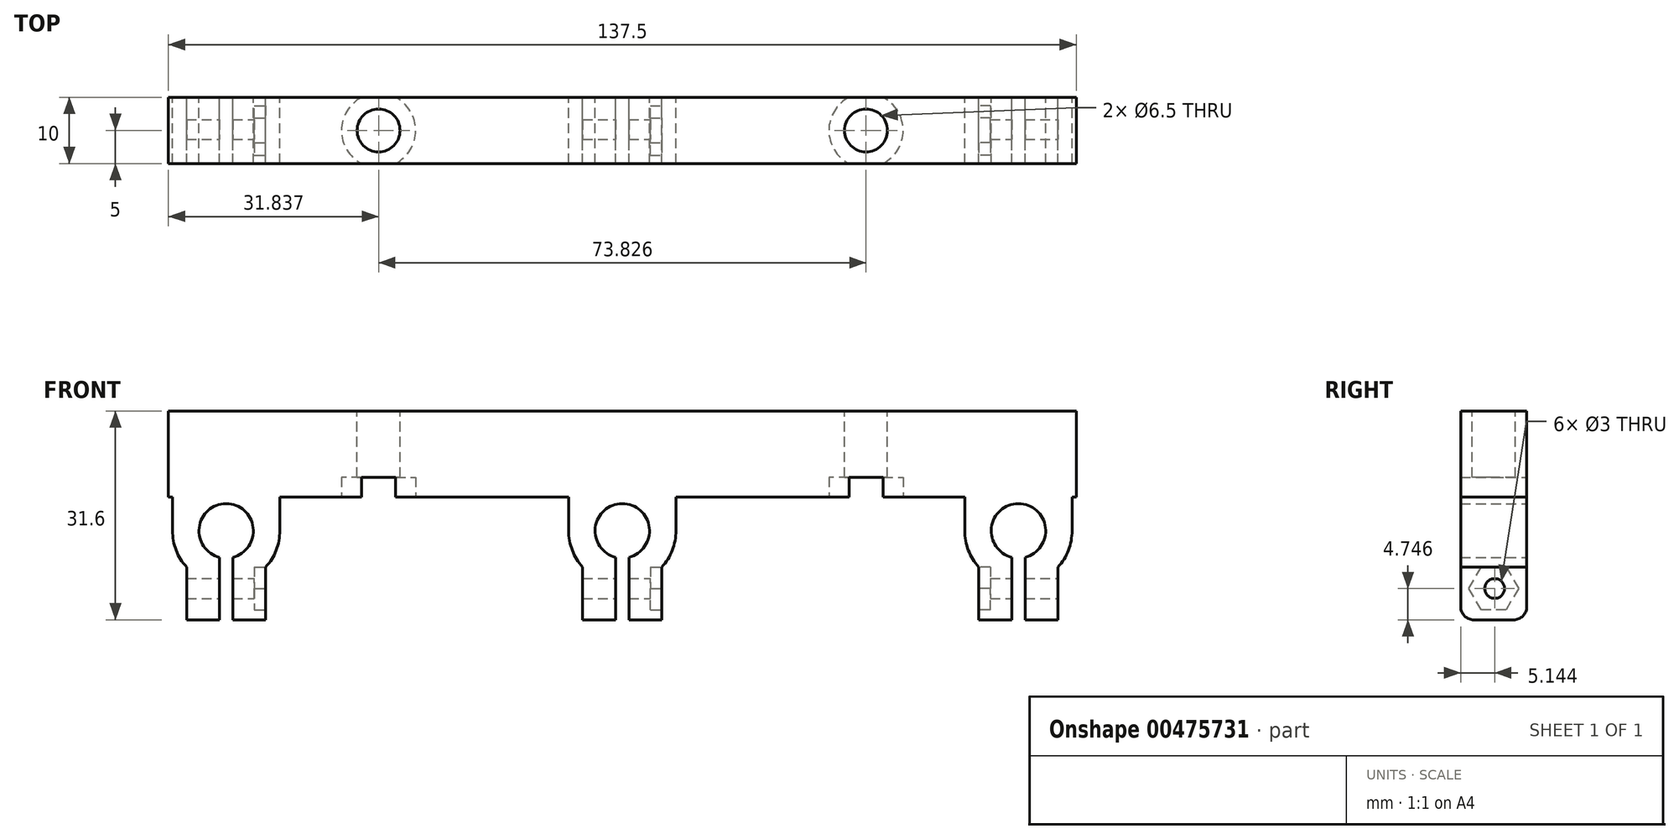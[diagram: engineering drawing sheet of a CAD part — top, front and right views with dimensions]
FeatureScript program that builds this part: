
annotation { "Feature Type Name" : "Feature", "Feature Type Description" : "" }
export const myFeature = defineFeature(function(context is Context, id is Id, definition is map)
    precondition{}
    {
        {
            var Q0;
            Q0=qCreatedBy(makeId("Top.planeOp"),FACE);
            var sketch = newSketch(context, id + "F0", { "sketchPlane" : qUnion([Q0])});
            skLineSegment(sketch, "E0.bottom", {"start": v(68.75, -5) * mm, "end": v(-68.75, -5) * mm});
            skLineSegment(sketch, "E0.top", {"start": v(68.75, 5) * mm, "end": v(-68.75, 5) * mm});
            skLineSegment(sketch, "E0.left", {"start": v(68.75, -5) * mm, "end": v(68.75, 5) * mm});
            skLineSegment(sketch, "E0.right", {"start": v(-68.75, -5) * mm, "end": v(-68.75, 5) * mm});
            skPoint(sketch, "E0.middle", {"position": v(0, 0) * mm});
            skSolve(sketch);
        }
        {
            var Q0;
            Q0=qSketchRegion(id+"F0",true);
            extrude(context, id + "F1", {"entities" : qUnion([Q0]), "depth" : 9 * mm});
        }
        {
            var Q0;
            Q0=makeQuery(id+"F1.opExtrude","SWEPT_FACE",FACE,{"disambiguationData":[OSD([sQuery(id+"F0.wireOp",EDGE,"E0.top")])]});
            var sketch = newSketch(context, id + "F2", { "sketchPlane" : qUnion([Q0])});
            skCircle(sketch, "E1", {"center": v(0, -9.13) * mm, "radius": 4.12 * mm});
            skPoint(sketch, "E1.centerSnap0", {"position": v(0, 0) * mm});
            skCircle(sketch, "E2", {"center": v(-60, -9.12) * mm, "radius": 4.12 * mm});
            skCircle(sketch, "E3", {"center": v(60, -9.13) * mm, "radius": 4.12 * mm});
            skLineSegment(sketch, "E4", {"start": v(60, -9.13) * mm, "end": v(0, -9.13) * mm, "construction": true});
            skLineSegment(sketch, "E5", {"start": v(-60, -9.12) * mm, "end": v(0, -9.13) * mm, "construction": true});
            skArc(sketch, "E6", {"start": v(-68.12, -9.12) * mm, "mid": v(-60, -17.25) * mm, "end": v(-51.88, -9.12) * mm});
            skLineSegment(sketch, "E7", {"start": v(-68.12, -9.12) * mm, "end": v(-51.88, -9.12) * mm, "construction": true});
            skArc(sketch, "E8", {"start": v(-8.12, -9.13) * mm, "mid": v(0, -17.25) * mm, "end": v(8.12, -9.13) * mm});
            skLineSegment(sketch, "E9", {"start": v(-8.12, -9.12) * mm, "end": v(8.12, -9.13) * mm, "construction": true});
            skArc(sketch, "E10", {"start": v(51.88, -9.13) * mm, "mid": v(60, -17.25) * mm, "end": v(68.12, -9.13) * mm});
            skLineSegment(sketch, "E11", {"start": v(51.88, -9.13) * mm, "end": v(68.12, -9.13) * mm, "construction": true});
            skLineSegment(sketch, "E12", {"start": v(-68.12, -9.12) * mm, "end": v(-68.12, -4) * mm});
            skLineSegment(sketch, "E13", {"start": v(-51.88, -9.12) * mm, "end": v(-51.88, -4) * mm});
            skLineSegment(sketch, "E14", {"start": v(-8.12, -9.13) * mm, "end": v(-8.12, -4) * mm});
            skLineSegment(sketch, "E15", {"start": v(8.12, -9.13) * mm, "end": v(8.12, -4) * mm});
            skLineSegment(sketch, "E16", {"start": v(51.88, -9.13) * mm, "end": v(51.88, -4) * mm});
            skLineSegment(sketch, "E17", {"start": v(68.12, -9.13) * mm, "end": v(68.12, -4) * mm});
            skLineSegment(sketch, "E18", {"start": v(68.12, -4) * mm, "end": v(68.75, -4) * mm});
            skLineSegment(sketch, "E19", {"start": v(68.75, -4) * mm, "end": v(68.75, 0) * mm});
            skLineSegment(sketch, "E20", {"start": v(51.88, -4) * mm, "end": v(8.12, -4) * mm});
            skLineSegment(sketch, "E21", {"start": v(-8.12, -4) * mm, "end": v(-51.88, -4) * mm});
            skLineSegment(sketch, "E22", {"start": v(-68.12, -4) * mm, "end": v(-68.75, -4) * mm});
            skLineSegment(sketch, "E23", {"start": v(-68.75, -4) * mm, "end": v(-68.75, 0) * mm});
            skLineSegment(sketch, "E24.bottom", {"start": v(66, -14.6) * mm, "end": v(54, -14.6) * mm, "construction": true});
            skLineSegment(sketch, "E24.top", {"start": v(66, -22.6) * mm, "end": v(54, -22.6) * mm});
            skLineSegment(sketch, "E24.left", {"start": v(66, -14.6) * mm, "end": v(66, -22.6) * mm});
            skLineSegment(sketch, "E24.right", {"start": v(54, -14.6) * mm, "end": v(54, -22.6) * mm});
            skLineSegment(sketch, "E25.bottom", {"start": v(6, -14.6) * mm, "end": v(-6, -14.6) * mm, "construction": true});
            skLineSegment(sketch, "E25.top", {"start": v(6, -22.6) * mm, "end": v(-6, -22.6) * mm});
            skLineSegment(sketch, "E25.left", {"start": v(6, -14.6) * mm, "end": v(6, -22.6) * mm});
            skLineSegment(sketch, "E25.right", {"start": v(-6, -14.6) * mm, "end": v(-6, -22.6) * mm});
            skLineSegment(sketch, "E26.bottom", {"start": v(-54, -14.6) * mm, "end": v(-66, -14.6) * mm, "construction": true});
            skLineSegment(sketch, "E26.top", {"start": v(-54, -22.6) * mm, "end": v(-66, -22.6) * mm});
            skLineSegment(sketch, "E26.left", {"start": v(-54, -14.6) * mm, "end": v(-54, -22.6) * mm});
            skLineSegment(sketch, "E26.right", {"start": v(-66, -14.6) * mm, "end": v(-66, -22.6) * mm});
            skLineSegment(sketch, "E27.bottom", {"start": v(61, -13.13) * mm, "end": v(59, -13.13) * mm});
            skLineSegment(sketch, "E27.top", {"start": v(61, -22.6) * mm, "end": v(59, -22.6) * mm});
            skLineSegment(sketch, "E27.left", {"start": v(61, -13.13) * mm, "end": v(61, -22.6) * mm});
            skLineSegment(sketch, "E27.right", {"start": v(59, -13.13) * mm, "end": v(59, -22.6) * mm});
            skLineSegment(sketch, "E28.bottom", {"start": v(1, -13.13) * mm, "end": v(-1, -13.13) * mm});
            skLineSegment(sketch, "E28.top", {"start": v(1, -22.6) * mm, "end": v(-1, -22.6) * mm});
            skLineSegment(sketch, "E28.left", {"start": v(1, -13.13) * mm, "end": v(1, -22.6) * mm});
            skLineSegment(sketch, "E28.right", {"start": v(-1, -13.13) * mm, "end": v(-1, -22.6) * mm});
            skLineSegment(sketch, "E29.bottom", {"start": v(-59, -13.13) * mm, "end": v(-61, -13.13) * mm});
            skLineSegment(sketch, "E29.top", {"start": v(-59, -22.6) * mm, "end": v(-61, -22.6) * mm});
            skLineSegment(sketch, "E29.left", {"start": v(-59, -13.13) * mm, "end": v(-59, -22.6) * mm});
            skLineSegment(sketch, "E29.right", {"start": v(-61, -13.13) * mm, "end": v(-61, -22.6) * mm});
            skSolve(sketch);
        }
        {
            var Q0;
            {var subQ0=sQuery(id+"F2.wireOp",EDGE,"E26.right");Q0=makeQuery(id+"F2.imprint","IMPRINT",FACE,{"disambiguationData":[TD([[makeQuery(id+"F2.imprint","IMPRINT",EDGE,{"derivedFrom":subQ0}),1.0]])]});}
            var Q1;
            {var subQ0=sQuery(id+"F2.wireOp",EDGE,"E26.left");Q1=makeQuery(id+"F2.imprint","IMPRINT",FACE,{"disambiguationData":[TD([[makeQuery(id+"F2.imprint","IMPRINT",EDGE,{"derivedFrom":subQ0}),-1.0]])]});}
            var Q2;
            {var subQ0=sQuery(id+"F2.wireOp",EDGE,"E25.right");Q2=makeQuery(id+"F2.imprint","IMPRINT",FACE,{"disambiguationData":[TD([[makeQuery(id+"F2.imprint","IMPRINT",EDGE,{"derivedFrom":subQ0}),1.0]])]});}
            var Q3;
            {var subQ0=sQuery(id+"F2.wireOp",EDGE,"E25.left");Q3=makeQuery(id+"F2.imprint","IMPRINT",FACE,{"disambiguationData":[TD([[makeQuery(id+"F2.imprint","IMPRINT",EDGE,{"derivedFrom":subQ0}),-1.0]])]});}
            var Q4;
            {var subQ0=sQuery(id+"F2.wireOp",EDGE,"E24.right");Q4=makeQuery(id+"F2.imprint","IMPRINT",FACE,{"disambiguationData":[TD([[makeQuery(id+"F2.imprint","IMPRINT",EDGE,{"derivedFrom":subQ0}),1.0]])]});}
            var Q5;
            {var subQ0=sQuery(id+"F2.wireOp",EDGE,"E24.left");Q5=makeQuery(id+"F2.imprint","IMPRINT",FACE,{"disambiguationData":[TD([[makeQuery(id+"F2.imprint","IMPRINT",EDGE,{"derivedFrom":subQ0}),-1.0]])]});}
            var Q6;
            {var subQ3=sQuery(id+"F2.wireOp",EDGE,"E12");Q6=makeQuery(id+"F2.imprint","IMPRINT",FACE,{"disambiguationData":[TD([[makeQuery(id+"F2.imprint","IMPRINT",EDGE,{"derivedFrom":subQ3}),-1.0]])]});}
            var Q7;
            Q7=makeQuery(id+"F1.opExtrude","SWEPT_FACE",FACE,{"disambiguationData":[OSD([sQuery(id+"F0.wireOp",EDGE,"E0.bottom")])]});
            extrude(context, id + "F3", {"entities" : qUnion([Q0, Q1, Q2, Q3, Q4, Q5, Q6]), "operationType" : NewBodyOperationType.ADD, "endBound" : BoundingType.UP_TO_SURFACE, "oppositeDirection" : true, "endBoundEntityFace" : qUnion([Q7]), "depth" : 10 * mm});
        }
        {
            var Q0;
            Q0=makeQuery(id+"F3.opExtrude","SWEPT_FACE",FACE,{"disambiguationData":[OSD([sQuery(id+"F2.wireOp",EDGE,"E26.left")])]});
            var sketch = newSketch(context, id + "F4", { "sketchPlane" : qUnion([Q0])});
            skCircle(sketch, "E30.cCircle", {"center": v(0, -17.85) * mm, "radius": 3.25 * mm, "construction": true});
            skPoint(sketch, "E30.cCircle.centerSnap1", {"position": v(0, -14.6) * mm});
            skLineSegment(sketch, "E30.0", {"start": v(1.88, -14.6) * mm, "end": v(3.75, -17.85) * mm});
            skLineSegment(sketch, "E30.1", {"start": v(3.75, -17.85) * mm, "end": v(1.88, -21.1) * mm});
            skLineSegment(sketch, "E30.2", {"start": v(1.88, -21.1) * mm, "end": v(-1.88, -21.1) * mm});
            skLineSegment(sketch, "E30.3", {"start": v(-1.88, -21.1) * mm, "end": v(-3.75, -17.85) * mm});
            skLineSegment(sketch, "E30.4", {"start": v(-3.75, -17.85) * mm, "end": v(-1.88, -14.6) * mm});
            skLineSegment(sketch, "E30.5", {"start": v(-1.88, -14.6) * mm, "end": v(1.88, -14.6) * mm});
            skPoint(sketch, "E30.0.midPoint", {"position": v(2.81, -16.23) * mm});
            skLineSegment(sketch, "E31.0", {"start": v(5, -14.6) * mm, "end": v(-5, -14.6) * mm});
            skSolve(sketch);
        }
        {
            var Q0;
            Q0=qSketchRegion(id+"F4",true);
            extrude(context, id + "F5", {"entities" : qUnion([Q0]), "operationType" : NewBodyOperationType.REMOVE, "oppositeDirection" : true, "depth" : 1.75 * mm});
        }
        {
            var Q0;
            Q0=makeQuery(id+"F3.opExtrude","SWEPT_FACE",FACE,{"disambiguationData":[OSD([sQuery(id+"F2.wireOp",EDGE,"E25.right")])]});
            var sketch = newSketch(context, id + "F6", { "sketchPlane" : qUnion([Q0])});
            skLineSegment(sketch, "E32.0.0", {"start": v(1.88, -14.6) * mm, "end": v(3.75, -17.85) * mm});
            skLineSegment(sketch, "E32.0.1", {"start": v(3.75, -17.85) * mm, "end": v(1.88, -21.1) * mm});
            skLineSegment(sketch, "E32.0.2", {"start": v(1.88, -21.1) * mm, "end": v(-1.88, -21.1) * mm});
            skLineSegment(sketch, "E32.0.3", {"start": v(-1.88, -21.1) * mm, "end": v(-3.75, -17.85) * mm});
            skLineSegment(sketch, "E32.0.4", {"start": v(-3.75, -17.85) * mm, "end": v(-1.88, -14.6) * mm});
            skLineSegment(sketch, "E32.0.5", {"start": v(-1.88, -14.6) * mm, "end": v(1.88, -14.6) * mm});
            skSolve(sketch);
        }
        {
            var Q0;
            Q0=qSketchRegion(id+"F6",true);
            extrude(context, id + "F7", {"entities" : qUnion([Q0]), "operationType" : NewBodyOperationType.REMOVE, "oppositeDirection" : true, "depth" : 1.75 * mm});
        }
        {
            var Q0;
            Q0=makeQuery(id+"F3.opExtrude","SWEPT_FACE",FACE,{"disambiguationData":[OSD([sQuery(id+"F2.wireOp",EDGE,"E24.right")])]});
            var sketch = newSketch(context, id + "F8", { "sketchPlane" : qUnion([Q0])});
            skLineSegment(sketch, "E33.0.0", {"start": v(-1.88, -14.6) * mm, "end": v(-3.75, -17.85) * mm});
            skLineSegment(sketch, "E33.0.1", {"start": v(-3.75, -17.85) * mm, "end": v(-1.88, -21.1) * mm});
            skLineSegment(sketch, "E33.0.2", {"start": v(-1.88, -21.1) * mm, "end": v(1.88, -21.1) * mm});
            skLineSegment(sketch, "E33.0.3", {"start": v(1.88, -21.1) * mm, "end": v(3.75, -17.85) * mm});
            skLineSegment(sketch, "E33.0.4", {"start": v(3.75, -17.85) * mm, "end": v(1.88, -14.6) * mm});
            skLineSegment(sketch, "E33.0.5", {"start": v(1.88, -14.6) * mm, "end": v(-1.88, -14.6) * mm});
            skSolve(sketch);
        }
        {
            var Q0;
            Q0=qSketchRegion(id+"F8",true);
            extrude(context, id + "F9", {"entities" : qUnion([Q0]), "operationType" : NewBodyOperationType.REMOVE, "oppositeDirection" : true, "depth" : 1.75 * mm});
        }
        {
            var Q0;
            Q0=makeQuery(id+"F3.opExtrude","SWEPT_FACE",FACE,{"disambiguationData":[OSD([sQuery(id+"F2.wireOp",EDGE,"E26.right")])]});
            var sketch = newSketch(context, id + "F10", { "sketchPlane" : qUnion([Q0])});
            skCircle(sketch, "E34", {"center": v(0.14, -17.85) * mm, "radius": 1.5 * mm});
            skPoint(sketch, "E34.centerSnap0", {"position": v(-3.75, -17.85) * mm});
            skSolve(sketch);
        }
        {
            var Q0;
            Q0=qSketchRegion(id+"F10",true);
            extrude(context, id + "F11", {"entities" : qUnion([Q0]), "operationType" : NewBodyOperationType.REMOVE, "endBound" : BoundingType.THROUGH_ALL, "oppositeDirection" : true, "depth" : 25 * mm});
        }
        {
            var Q0;
            Q0=makeQuery(id+"F1.opExtrude","CAP_FACE",FACE,{"disambiguationData":[OSD([sQuery(id+"F0.wireOp",EDGE,"E0.bottom"),sQuery(id+"F0.wireOp",EDGE,"E0.top"),sQuery(id+"F0.wireOp",EDGE,"E0.left"),sQuery(id+"F0.wireOp",EDGE,"E0.right")])],"isStart":false});
            var sketch = newSketch(context, id + "F12", { "sketchPlane" : qUnion([Q0])});
            skCircle(sketch, "E35", {"center": v(36.91, 0) * mm, "radius": 3.25 * mm});
            skLineSegment(sketch, "E36", {"start": v(0, 0) * mm, "end": v(36.91, 0) * mm, "construction": true});
            skCircle(sketch, "E37", {"center": v(-36.91, 0) * mm, "radius": 3.25 * mm});
            skLineSegment(sketch, "E38", {"start": v(0, 0) * mm, "end": v(-36.91, 0) * mm, "construction": true});
            skSolve(sketch);
        }
        {
            var Q0;
            Q0=qSketchRegion(id+"F12",true);
            extrude(context, id + "F13", {"entities" : qUnion([Q0]), "operationType" : NewBodyOperationType.REMOVE, "endBound" : BoundingType.THROUGH_ALL, "oppositeDirection" : true, "depth" : 25 * mm});
        }
        {
            var Q0;
            Q0=makeQuery(id+"F3.opExtrude","SWEPT_FACE",FACE,{"disambiguationData":[OSD([sQuery(id+"F2.wireOp",EDGE,"E26.right")])]});
            var sketch = newSketch(context, id + "F14", { "sketchPlane" : qUnion([Q0])});
            skArc(sketch, "E39", {"start": v(-5, -20.6) * mm, "mid": v(-4.41, -22.02) * mm, "end": v(-3, -22.6) * mm});
            skArc(sketch, "E40", {"start": v(3, -22.6) * mm, "mid": v(4.41, -22.02) * mm, "end": v(5, -20.6) * mm});
            skSolve(sketch);
        }
        {
            var Q0;
            Q0=qSketchRegion(id+"F14",true);
            var Q1;
            {var subQ0=sQuery(id+"F14.wireOp",EDGE,"E39");Q1=makeQuery(id+"F14.imprint","IMPRINT",FACE,{"disambiguationData":[TD([[makeQuery(id+"F14.imprint","IMPRINT",EDGE,{"derivedFrom":subQ0}),-1.0]])]});}
            var Q2;
            {var subQ0=sQuery(id+"F14.wireOp",EDGE,"E40");Q2=makeQuery(id+"F14.imprint","IMPRINT",FACE,{"disambiguationData":[TD([[makeQuery(id+"F14.imprint","IMPRINT",EDGE,{"derivedFrom":subQ0}),-1.0]])]});}
            extrude(context, id + "F15", {"entities" : qUnion([Q0, Q1, Q2]), "operationType" : NewBodyOperationType.REMOVE, "endBound" : BoundingType.THROUGH_ALL, "oppositeDirection" : true, "depth" : 25 * mm});
        }
        {
            var Q0;
            Q0=makeQuery(id+"F3.opExtrude","SWEPT_FACE",FACE,{"disambiguationData":[OSD([sQuery(id+"F2.wireOp",EDGE,"E21")])]});
            var sketch = newSketch(context, id + "F16", { "sketchPlane" : qUnion([Q0])});
            skCircle(sketch, "E41.0", {"center": v(36.91, 0) * mm, "radius": 3.25 * mm});
            skCircle(sketch, "E41.1", {"center": v(-36.91, 0) * mm, "radius": 3.25 * mm});
            skCircle(sketch, "E42", {"center": v(-36.91, 0) * mm, "radius": 5.62 * mm});
            skCircle(sketch, "E43", {"center": v(36.91, 0) * mm, "radius": 5.62 * mm});
            skSolve(sketch);
        }
        {
            var Q0;
            Q0=qSketchRegion(id+"F16",true);
            extrude(context, id + "F17", {"entities" : qUnion([Q0]), "operationType" : NewBodyOperationType.REMOVE, "oppositeDirection" : true, "depth" : 3 * mm});
        }
    });
